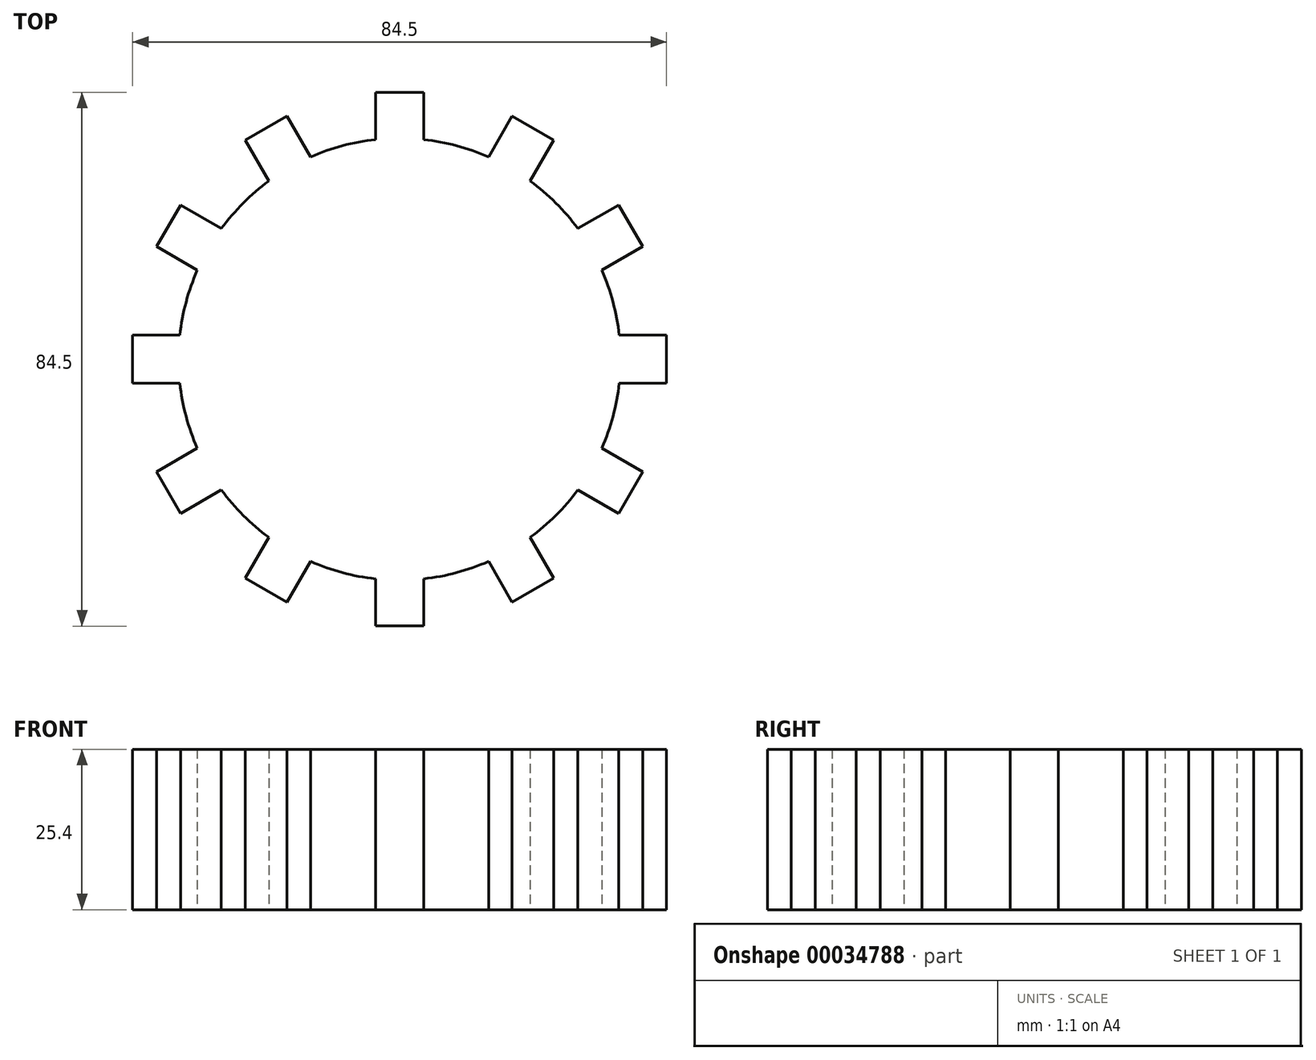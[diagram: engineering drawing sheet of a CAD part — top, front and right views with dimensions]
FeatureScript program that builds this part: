
annotation { "Feature Type Name" : "Feature", "Feature Type Description" : "" }
export const myFeature = defineFeature(function(context is Context, id is Id, definition is map)
    precondition{}
    {
        {
            var Q0;
            Q0=qCreatedBy(makeId("Top.planeOp"),FACE);
            var sketch = newSketch(context, id + "F0", { "sketchPlane" : qUnion([Q0])});
            skCircle(sketch, "E0", {"center": v(0, 0) * mm, "radius": 34.98 * mm});
            skLineSegment(sketch, "E1.rect.bottom", {"start": v(42.25, 3.81) * mm, "end": v(27.71, 3.81) * mm});
            skLineSegment(sketch, "E1.rect.top", {"start": v(42.25, -3.81) * mm, "end": v(27.71, -3.81) * mm});
            skLineSegment(sketch, "E1.rect.left", {"start": v(42.25, 3.81) * mm, "end": v(42.25, -3.81) * mm});
            skLineSegment(sketch, "E1.rect.right", {"start": v(27.71, 3.81) * mm, "end": v(27.71, -3.81) * mm});
            skPoint(sketch, "E1.rect.middle", {"position": v(34.98, 0) * mm});
            skLineSegment(sketch, "E2.1.0", {"start": v(34.68, 24.42) * mm, "end": v(22.1, 17.16) * mm});
            skLineSegment(sketch, "E2.1.1", {"start": v(34.68, 24.42) * mm, "end": v(38.5, 17.82) * mm});
            skLineSegment(sketch, "E2.1.2", {"start": v(38.5, 17.82) * mm, "end": v(25.9, 10.56) * mm});
            skLineSegment(sketch, "E2.2.0", {"start": v(17.82, 38.5) * mm, "end": v(10.56, 25.9) * mm});
            skLineSegment(sketch, "E2.2.1", {"start": v(17.82, 38.5) * mm, "end": v(24.42, 34.68) * mm});
            skLineSegment(sketch, "E2.2.2", {"start": v(24.42, 34.68) * mm, "end": v(17.16, 22.1) * mm});
            skLineSegment(sketch, "E2.3.0", {"start": v(-3.8, 42.25) * mm, "end": v(-3.8, 27.71) * mm});
            skLineSegment(sketch, "E2.3.1", {"start": v(-3.81, 42.25) * mm, "end": v(3.81, 42.25) * mm});
            skLineSegment(sketch, "E2.3.2", {"start": v(3.8, 42.25) * mm, "end": v(3.8, 27.71) * mm});
            skLineSegment(sketch, "E2.4.0", {"start": v(-24.42, 34.68) * mm, "end": v(-17.16, 22.1) * mm});
            skLineSegment(sketch, "E2.4.1", {"start": v(-24.42, 34.68) * mm, "end": v(-17.82, 38.5) * mm});
            skLineSegment(sketch, "E2.4.2", {"start": v(-17.82, 38.5) * mm, "end": v(-10.56, 25.9) * mm});
            skLineSegment(sketch, "E2.5.0", {"start": v(-38.5, 17.82) * mm, "end": v(-25.9, 10.56) * mm});
            skLineSegment(sketch, "E2.5.1", {"start": v(-38.5, 17.82) * mm, "end": v(-34.68, 24.42) * mm});
            skLineSegment(sketch, "E2.5.2", {"start": v(-34.68, 24.42) * mm, "end": v(-22.1, 17.16) * mm});
            skLineSegment(sketch, "E2.6.0", {"start": v(-42.25, -3.8) * mm, "end": v(-27.71, -3.8) * mm});
            skLineSegment(sketch, "E2.6.1", {"start": v(-42.25, -3.8) * mm, "end": v(-42.25, 3.81) * mm});
            skLineSegment(sketch, "E2.6.2", {"start": v(-42.25, 3.81) * mm, "end": v(-27.71, 3.81) * mm});
            skLineSegment(sketch, "E2.7.0", {"start": v(-34.68, -24.42) * mm, "end": v(-22.1, -17.16) * mm});
            skLineSegment(sketch, "E2.7.1", {"start": v(-34.68, -24.42) * mm, "end": v(-38.5, -17.82) * mm});
            skLineSegment(sketch, "E2.7.2", {"start": v(-38.5, -17.82) * mm, "end": v(-25.9, -10.56) * mm});
            skLineSegment(sketch, "E2.8.0", {"start": v(-17.82, -38.5) * mm, "end": v(-10.56, -25.9) * mm});
            skLineSegment(sketch, "E2.8.1", {"start": v(-17.82, -38.5) * mm, "end": v(-24.42, -34.68) * mm});
            skLineSegment(sketch, "E2.8.2", {"start": v(-24.42, -34.68) * mm, "end": v(-17.16, -22.1) * mm});
            skLineSegment(sketch, "E2.9.0", {"start": v(3.8, -42.25) * mm, "end": v(3.8, -27.71) * mm});
            skLineSegment(sketch, "E2.9.1", {"start": v(3.8, -42.25) * mm, "end": v(-3.81, -42.25) * mm});
            skLineSegment(sketch, "E2.9.2", {"start": v(-3.81, -42.25) * mm, "end": v(-3.81, -27.71) * mm});
            skLineSegment(sketch, "E2.10.0", {"start": v(24.42, -34.68) * mm, "end": v(17.16, -22.1) * mm});
            skLineSegment(sketch, "E2.10.1", {"start": v(24.42, -34.68) * mm, "end": v(17.82, -38.5) * mm});
            skLineSegment(sketch, "E2.10.2", {"start": v(17.82, -38.5) * mm, "end": v(10.56, -25.9) * mm});
            skLineSegment(sketch, "E2.11.0", {"start": v(38.5, -17.82) * mm, "end": v(25.9, -10.56) * mm});
            skLineSegment(sketch, "E2.11.1", {"start": v(38.5, -17.82) * mm, "end": v(34.68, -24.42) * mm});
            skLineSegment(sketch, "E2.11.2", {"start": v(34.68, -24.42) * mm, "end": v(22.1, -17.16) * mm});
            skSolve(sketch);
        }
        {
            var Q0;
            Q0 = qSketchRegion(id + "F0", true);
            extrude(context, id + "F1", {"entities" : qUnion([Q0]), "depth" : 25.4 * mm});
        }
    });
